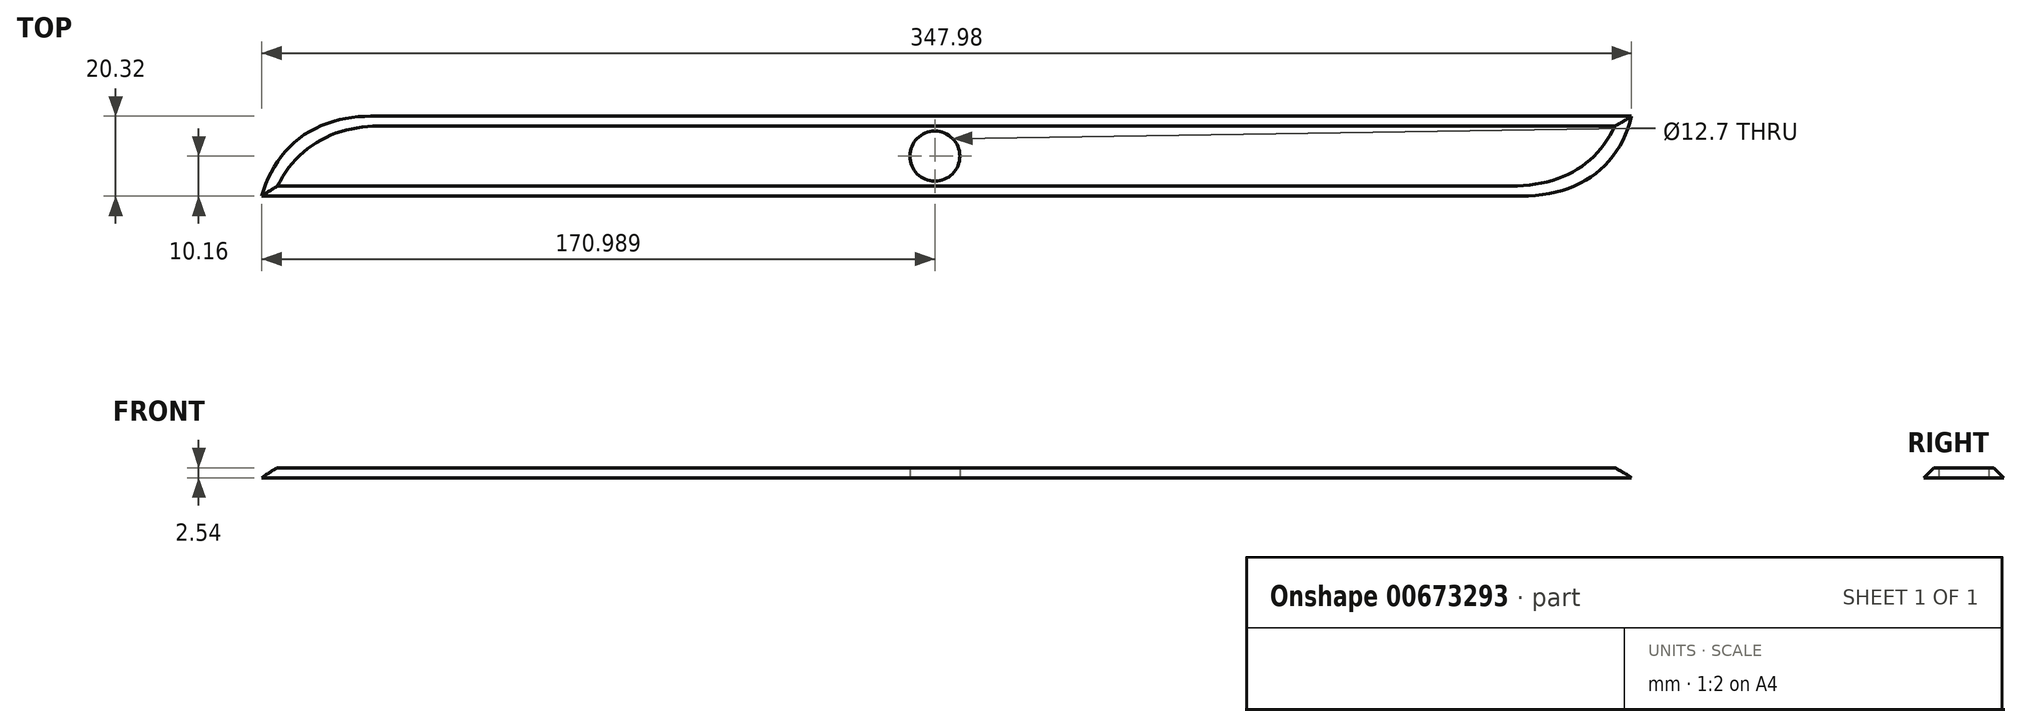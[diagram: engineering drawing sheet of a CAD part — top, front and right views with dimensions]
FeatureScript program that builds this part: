
annotation { "Feature Type Name" : "Feature", "Feature Type Description" : "" }
export const myFeature = defineFeature(function(context is Context, id is Id, definition is map)
    precondition{}
    {
        {
            var Q0;
            Q0=qCreatedBy(makeId("Top.planeOp"),FACE);
            var sketch = newSketch(context, id + "F0", { "sketchPlane" : qUnion([Q0])});
            skLineSegment(sketch, "E0.bottom", {"start": v(-173.83, -25.4) * mm, "end": v(180.86, -25.4) * mm});
            skLineSegment(sketch, "E0.top", {"start": v(-173.83, 0) * mm, "end": v(180.86, 0) * mm});
            skLineSegment(sketch, "E0.left", {"start": v(-173.83, -25.4) * mm, "end": v(-173.83, 0) * mm});
            skLineSegment(sketch, "E0.right", {"start": v(180.86, -25.4) * mm, "end": v(180.86, 0) * mm});
            skSolve(sketch);
        }
        {
            var Q0;
            Q0=makeQuery(id+"F0.imprint","IMPRINT",FACE,{"disambiguationData":[TD([[makeQuery(id+"F0.imprint","IMPRINT",EDGE,{"derivedFrom":sQuery(id+"F0.wireOp",EDGE,"E0.bottom")}),1.0]])]});
            extrude(context, id + "F1", {"entities" : qUnion([Q0]), "depth" : 2.54 * mm, "offsetDistance" : 25.4 * mm});
        }
        {
            var Q0;
            Q0=makeQuery(id+"F1.opExtrude","CAP_EDGE",EDGE,{"disambiguationData":[OSD([sQuery(id+"F0.wireOp",EDGE,"E0.left")])],"isStart":false});
            var Q1;
            Q1=makeQuery(id+"F1.opExtrude","CAP_EDGE",EDGE,{"disambiguationData":[OSD([sQuery(id+"F0.wireOp",EDGE,"E0.top")])],"isStart":false});
            chamfer(context, id + "F2", {"entities" : qUnion([Q0, Q1]), "width" : 5.08 * mm, "tangentPropagation" : true});
        }
        {
            var Q0;
            Q0=makeQuery(id+"F2.opChamfer","BLEND_EDGE",EDGE,{"blendedFrom":[makeQuery(id+"F1.opExtrude","CAP_EDGE",EDGE,{"disambiguationData":[OSD([sQuery(id+"F0.wireOp",EDGE,"E0.top")])],"isStart":false}),makeQuery(id+"F1.opExtrude","CAP_EDGE",EDGE,{"disambiguationData":[OSD([sQuery(id+"F0.wireOp",EDGE,"E0.left")])],"isStart":false})],"blendedInto":[]});
            fillet(context, id + "F3", {"entities" : qUnion([Q0]), "radius" : 41.05 * mm, "tangentPropagation" : true, "allowEdgeOverflow" : false});
        }
        {
            var Q0;
            Q0=makeQuery(id+"F1.opExtrude","CAP_EDGE",EDGE,{"disambiguationData":[OSD([sQuery(id+"F0.wireOp",EDGE,"E0.bottom")])],"isStart":false});
            var Q1;
            Q1=makeQuery(id+"F1.opExtrude","CAP_EDGE",EDGE,{"disambiguationData":[OSD([sQuery(id+"F0.wireOp",EDGE,"E0.right")])],"isStart":false});
            chamfer(context, id + "F4", {"entities" : qUnion([Q0, Q1]), "width" : 5.08 * mm, "tangentPropagation" : true});
        }
        {
            var Q0;
            Q0=makeQuery(id+"F4.opChamfer","BLEND_EDGE",EDGE,{"blendedFrom":[makeQuery(id+"F1.opExtrude","CAP_EDGE",EDGE,{"disambiguationData":[OSD([sQuery(id+"F0.wireOp",EDGE,"E0.bottom")])],"isStart":false}),makeQuery(id+"F1.opExtrude","CAP_EDGE",EDGE,{"disambiguationData":[OSD([sQuery(id+"F0.wireOp",EDGE,"E0.right")])],"isStart":false})],"blendedInto":[]});
            fillet(context, id + "F5", {"entities" : qUnion([Q0]), "radius" : 41.05 * mm, "tangentPropagation" : true, "allowEdgeOverflow" : false});
        }
        {
            var Q0;
            Q0=qCreatedBy(makeId("Top.planeOp"),FACE);
            var sketch = newSketch(context, id + "F6", { "sketchPlane" : qUnion([Q0])});
            skCircle(sketch, "E1", {"center": v(0.35, -12.7) * mm, "radius": 6.35 * mm});
            skPoint(sketch, "E1.first.point", {"position": v(0, -6.36) * mm});
            skPoint(sketch, "E1.second.point", {"position": v(0, -19.04) * mm});
            skPoint(sketch, "E1.third.point", {"position": v(6.7, -12.8) * mm});
            skSolve(sketch);
        }
        {
            var Q0;
            Q0 = qSketchRegion(id + "F6", true);
            extrude(context, id + "F7", {"entities" : qUnion([Q0]), "operationType" : NewBodyOperationType.REMOVE, "oppositeDirection" : true, "depth" : -2.54 * mm, "offsetDistance" : 25.4 * mm});
        }
    });
